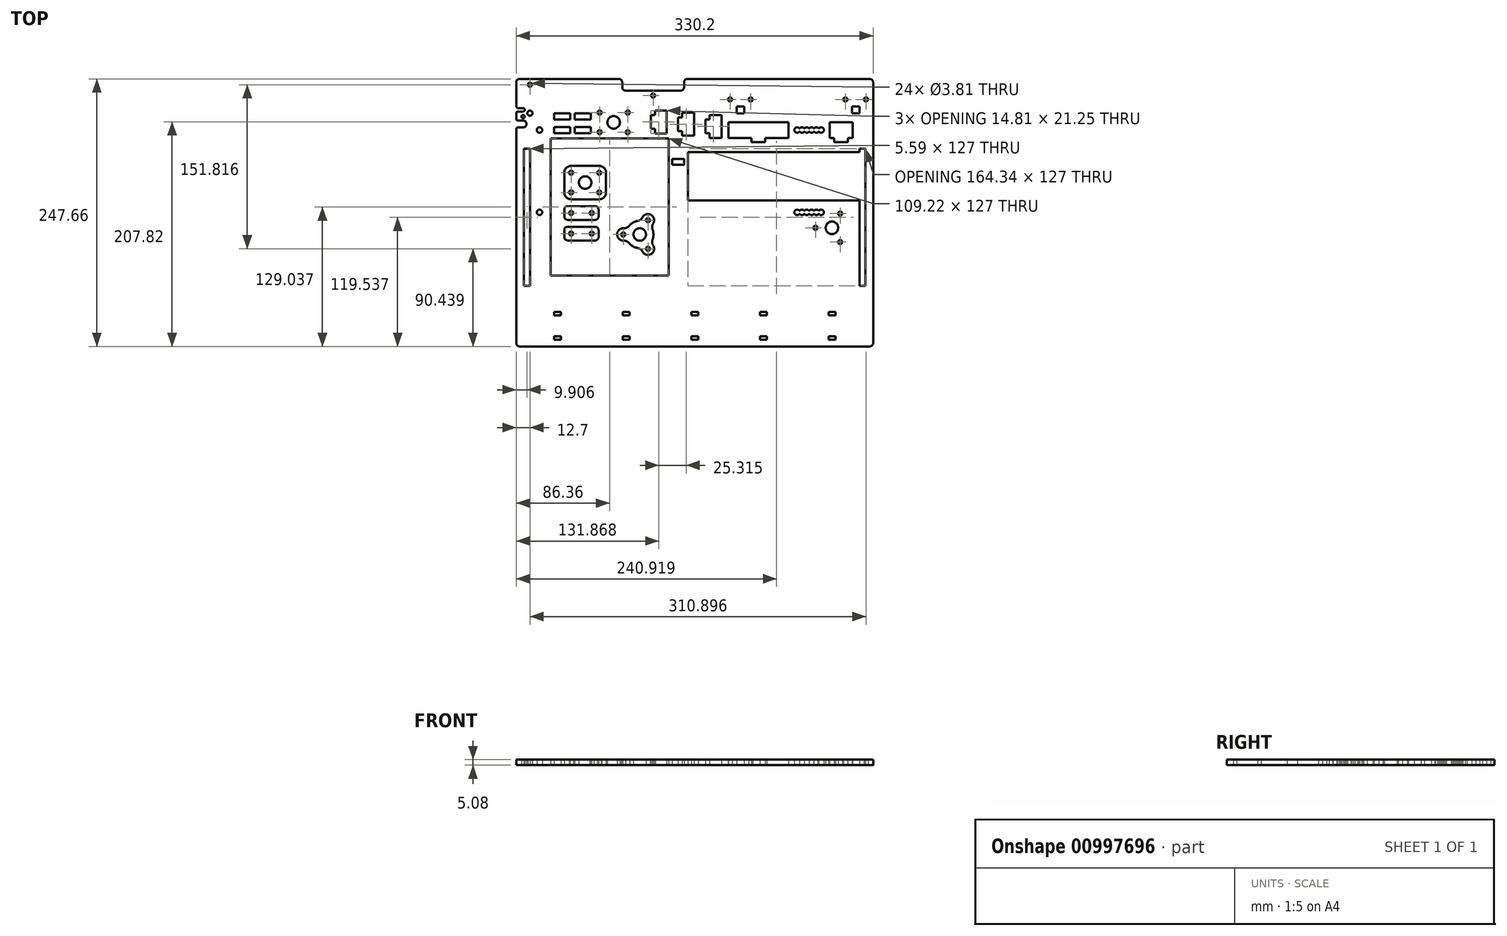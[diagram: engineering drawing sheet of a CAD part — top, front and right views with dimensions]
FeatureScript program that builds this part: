
annotation { "Feature Type Name" : "Feature", "Feature Type Description" : "" }
export const myFeature = defineFeature(function(context is Context, id is Id, definition is map)
    precondition{}
    {
        {
            var Q0;
            Q0=qCreatedBy(makeId("Top.planeOp"),FACE);
            var sketch = newSketch(context, id + "F0", { "sketchPlane" : qUnion([Q0])});
            skLineSegment(sketch, "E0.bottom", {"start": v(165.1, 111.12) * mm, "end": v(-165.1, 111.12) * mm, "construction": true});
            skLineSegment(sketch, "E0.top", {"start": v(161.93, -111.12) * mm, "end": v(-161.93, -111.12) * mm});
            skLineSegment(sketch, "E0.left", {"start": v(165.1, 111.13) * mm, "end": v(165.1, -107.95) * mm});
            skLineSegment(sketch, "E0.right", {"start": v(-165.1, 111.13) * mm, "end": v(-165.1, 111.12) * mm});
            skPoint(sketch, "E0.middle", {"position": v(0, 0) * mm});
            skLineSegment(sketch, "E1.bottom", {"start": v(86.87, 96.52) * mm, "end": v(31.15, 96.52) * mm});
            skLineSegment(sketch, "E1.top", {"start": v(86.87, 81.92) * mm, "end": v(65.36, 81.92) * mm});
            skLineSegment(sketch, "E1.left", {"start": v(86.87, 96.52) * mm, "end": v(86.87, 81.92) * mm});
            skLineSegment(sketch, "E1.right", {"start": v(31.15, 96.52) * mm, "end": v(31.15, 81.91) * mm});
            skPoint(sketch, "E1.middle", {"position": v(59.01, 89.22) * mm});
            skLineSegment(sketch, "E2.bottom", {"start": v(146.05, 96.52) * mm, "end": v(124.97, 96.52) * mm});
            skLineSegment(sketch, "E2.top", {"start": v(146.05, 81.92) * mm, "end": v(141.86, 81.92) * mm});
            skLineSegment(sketch, "E2.left", {"start": v(146.05, 96.52) * mm, "end": v(146.05, 81.91) * mm});
            skLineSegment(sketch, "E2.right", {"start": v(124.97, 96.52) * mm, "end": v(124.97, 81.91) * mm});
            skPoint(sketch, "E2.middle", {"position": v(135.5, 89.22) * mm});
            skPoint(sketch, "E2.middle.positionSnap0", {"position": v(86.87, 89.22) * mm});
            skPoint(sketch, "E2.centerSnap0", {"position": v(86.87, 89.22) * mm});
            skLineSegment(sketch, "E3", {"start": v(52.66, 81.91) * mm, "end": v(52.66, 78.1) * mm});
            skLineSegment(sketch, "E4", {"start": v(52.66, 78.1) * mm, "end": v(65.36, 78.1) * mm});
            skLineSegment(sketch, "E5", {"start": v(65.36, 78.1) * mm, "end": v(65.36, 81.91) * mm});
            skPoint(sketch, "E6", {"position": v(59.01, 78.1) * mm});
            skLineSegment(sketch, "E7", {"start": v(59.01, 96.52) * mm, "end": v(59.01, 78.1) * mm, "construction": true});
            skLineSegment(sketch, "E8", {"start": v(129.16, 81.91) * mm, "end": v(129.16, 78.1) * mm});
            skLineSegment(sketch, "E9", {"start": v(129.16, 78.1) * mm, "end": v(141.86, 78.1) * mm});
            skLineSegment(sketch, "E10", {"start": v(141.86, 78.1) * mm, "end": v(141.86, 81.91) * mm});
            skLineSegment(sketch, "E11", {"start": v(135.5, 78.1) * mm, "end": v(135.5, 96.52) * mm, "construction": true});
            skLineSegment(sketch, "E12.trimOffspring", {"start": v(52.66, 81.92) * mm, "end": v(31.15, 81.92) * mm});
            skLineSegment(sketch, "E13.trimOffspring", {"start": v(129.16, 81.92) * mm, "end": v(124.97, 81.92) * mm});
            skLineSegment(sketch, "E14", {"start": v(52.66, 81.92) * mm, "end": v(65.36, 81.92) * mm, "construction": true});
            skLineSegment(sketch, "E15", {"start": v(129.16, 81.92) * mm, "end": v(141.86, 81.92) * mm, "construction": true});
            skLineSegment(sketch, "E16.bottom", {"start": v(152.4, 68.7) * mm, "end": v(-6.35, 68.7) * mm});
            skLineSegment(sketch, "E16.top", {"start": v(152.4, 24.1) * mm, "end": v(-6.35, 24.1) * mm});
            skLineSegment(sketch, "E16.left", {"start": v(152.4, 68.7) * mm, "end": v(152.4, 24.1) * mm, "construction": true});
            skPoint(sketch, "E16.middle", {"position": v(73.02, 46.4) * mm});
            skLineSegment(sketch, "E17", {"start": v(-6.35, 68.7) * mm, "end": v(-6.35, 24.1) * mm});
            skArc(sketch, "E18", {"start": v(97.03, 90.45) * mm, "mid": v(92.27, 89.22) * mm, "end": v(97.03, 87.99) * mm});
            skArc(sketch, "E19.1.0.0", {"start": v(97.03, 87.99) * mm, "mid": v(99.25, 86.68) * mm, "end": v(101.47, 87.99) * mm});
            skArc(sketch, "E19.2.0.0", {"start": v(101.47, 87.99) * mm, "mid": v(103.7, 86.68) * mm, "end": v(105.92, 87.99) * mm});
            skArc(sketch, "E19.3.0.0", {"start": v(105.92, 87.99) * mm, "mid": v(108.14, 86.68) * mm, "end": v(110.36, 87.99) * mm});
            skArc(sketch, "E19.4.0.0", {"start": v(110.36, 87.99) * mm, "mid": v(112.59, 86.68) * mm, "end": v(114.8, 87.99) * mm});
            skArc(sketch, "E19.5.0.0", {"start": v(114.8, 87.99) * mm, "mid": v(119.57, 89.22) * mm, "end": v(114.8, 90.45) * mm});
            skLineSegment(sketch, "E19.direction1", {"start": v(94.8, 89.22) * mm, "end": v(99.25, 89.22) * mm, "construction": true});
            skLineSegment(sketch, "E20", {"start": v(94.8, 89.22) * mm, "end": v(117.03, 89.22) * mm, "construction": true});
            skArc(sketch, "E21.trimOffspring", {"start": v(101.47, 90.45) * mm, "mid": v(99.25, 91.76) * mm, "end": v(97.03, 90.45) * mm});
            skArc(sketch, "E22.trimOffspring", {"start": v(105.92, 90.45) * mm, "mid": v(103.7, 91.76) * mm, "end": v(101.47, 90.45) * mm});
            skArc(sketch, "E23.trimOffspring", {"start": v(110.36, 90.45) * mm, "mid": v(108.14, 91.76) * mm, "end": v(105.92, 90.45) * mm});
            skArc(sketch, "E24.trimOffspring", {"start": v(114.8, 90.45) * mm, "mid": v(112.59, 91.76) * mm, "end": v(110.36, 90.45) * mm});
            skPoint(sketch, "E25", {"position": v(105.92, 89.22) * mm});
            skArc(sketch, "E26.1.0.0", {"start": v(114.8, 14.25) * mm, "mid": v(112.59, 15.56) * mm, "end": v(110.36, 14.25) * mm});
            skArc(sketch, "E26.1.0.1", {"start": v(97.03, 14.25) * mm, "mid": v(92.27, 13.02) * mm, "end": v(97.03, 11.79) * mm});
            skLineSegment(sketch, "E26.1.0.2", {"start": v(94.8, 13.02) * mm, "end": v(117.03, 13.02) * mm, "construction": true});
            skArc(sketch, "E26.1.0.3", {"start": v(105.92, 14.25) * mm, "mid": v(103.7, 15.56) * mm, "end": v(101.47, 14.25) * mm});
            skArc(sketch, "E26.1.0.4", {"start": v(110.36, 11.79) * mm, "mid": v(112.59, 10.48) * mm, "end": v(114.8, 11.79) * mm});
            skArc(sketch, "E26.1.0.5", {"start": v(114.8, 11.79) * mm, "mid": v(119.57, 13.02) * mm, "end": v(114.8, 14.25) * mm});
            skArc(sketch, "E26.1.0.6", {"start": v(97.03, 11.79) * mm, "mid": v(99.25, 10.48) * mm, "end": v(101.47, 11.79) * mm});
            skPoint(sketch, "E26.1.0.7", {"position": v(105.92, 13.02) * mm});
            skArc(sketch, "E26.1.0.8", {"start": v(110.36, 14.25) * mm, "mid": v(108.14, 15.56) * mm, "end": v(105.92, 14.25) * mm});
            skLineSegment(sketch, "E26.1.0.9", {"start": v(94.8, 13.02) * mm, "end": v(99.25, 13.02) * mm, "construction": true});
            skArc(sketch, "E26.1.0.10", {"start": v(101.47, 11.79) * mm, "mid": v(103.7, 10.48) * mm, "end": v(105.92, 11.79) * mm});
            skArc(sketch, "E26.1.0.11", {"start": v(105.92, 11.79) * mm, "mid": v(108.14, 10.48) * mm, "end": v(110.36, 11.79) * mm});
            skArc(sketch, "E26.1.0.12", {"start": v(101.47, 14.25) * mm, "mid": v(99.25, 15.56) * mm, "end": v(97.03, 14.25) * mm});
            skLineSegment(sketch, "E26.direction1", {"start": v(94.8, 89.22) * mm, "end": v(94.8, 13.02) * mm, "construction": true});
            skLineSegment(sketch, "E27", {"start": v(94.8, 89.22) * mm, "end": v(86.87, 89.22) * mm, "construction": true});
            skLineSegment(sketch, "E28.bottom", {"start": v(-24.13, 81.4) * mm, "end": v(-133.35, 81.4) * mm});
            skLineSegment(sketch, "E28.top", {"start": v(-24.13, -45.6) * mm, "end": v(-133.35, -45.6) * mm});
            skLineSegment(sketch, "E28.left", {"start": v(-24.13, 81.4) * mm, "end": v(-24.13, -45.6) * mm});
            skLineSegment(sketch, "E28.right", {"start": v(-133.35, 81.4) * mm, "end": v(-133.35, -45.6) * mm});
            skLineSegment(sketch, "E29", {"start": v(-165.1, 111.12) * mm, "end": v(-165.1, 133.35) * mm});
            skLineSegment(sketch, "E30", {"start": v(-161.93, 136.53) * mm, "end": v(-70.15, 136.53) * mm});
            skLineSegment(sketch, "E31", {"start": v(165.1, 133.35) * mm, "end": v(165.1, 111.12) * mm});
            skCircle(sketch, "E32", {"center": v(-152.4, 131.12) * mm, "radius": 1.9 * mm});
            skCircle(sketch, "E33", {"center": v(-38.4, 121.12) * mm, "radius": 1.9 * mm});
            skLineSegment(sketch, "E34", {"start": v(152.4, 68.7) * mm, "end": v(152.4, 71.9) * mm});
            skLineSegment(sketch, "E35", {"start": v(152.4, 71.9) * mm, "end": v(157.99, 71.9) * mm});
            skLineSegment(sketch, "E36", {"start": v(157.99, 71.9) * mm, "end": v(157.99, -55.1) * mm});
            skLineSegment(sketch, "E37", {"start": v(157.99, -55.1) * mm, "end": v(152.4, -55.1) * mm});
            skLineSegment(sketch, "E38", {"start": v(152.4, -55.1) * mm, "end": v(152.4, 24.1) * mm});
            skLineSegment(sketch, "E39.bottom", {"start": v(-157.99, 71.9) * mm, "end": v(-152.4, 71.9) * mm});
            skLineSegment(sketch, "E39.top", {"start": v(-157.99, -55.1) * mm, "end": v(-152.4, -55.1) * mm});
            skLineSegment(sketch, "E39.left", {"start": v(-157.99, 71.9) * mm, "end": v(-157.99, -55.1) * mm});
            skLineSegment(sketch, "E39.right", {"start": v(-152.4, 71.9) * mm, "end": v(-152.4, -55.1) * mm});
            skLineSegment(sketch, "E40", {"start": v(-152.4, -55.1) * mm, "end": v(152.4, -55.1) * mm, "construction": true});
            skCircle(sketch, "E41", {"center": v(-143.51, 89.22) * mm, "radius": 2.54 * mm});
            skCircle(sketch, "E42.1.0.0", {"center": v(-143.51, 13.02) * mm, "radius": 2.54 * mm});
            skLineSegment(sketch, "E42.direction1", {"start": v(-143.51, 89.22) * mm, "end": v(-143.51, 13.02) * mm, "construction": true});
            skLineSegment(sketch, "E43", {"start": v(-66.98, 133.35) * mm, "end": v(-66.98, 128.74) * mm});
            skLineSegment(sketch, "E44", {"start": v(-63.8, 125.57) * mm, "end": v(-13, 125.57) * mm});
            skLineSegment(sketch, "E45", {"start": v(-9.83, 128.75) * mm, "end": v(-9.83, 133.35) * mm});
            skPoint(sketch, "E46", {"position": v(-38.4, 125.57) * mm});
            skLineSegment(sketch, "E47", {"start": v(-38.4, 125.57) * mm, "end": v(-38.4, 121.12) * mm, "construction": true});
            skLineSegment(sketch, "E48.trimOffspring", {"start": v(-6.65, 136.53) * mm, "end": v(161.92, 136.53) * mm});
            skLineSegment(sketch, "E49", {"start": v(-66.98, 136.53) * mm, "end": v(-9.83, 136.53) * mm, "construction": true});
            skPoint(sketch, "E50.visualSharp", {"position": v(-165.1, 136.53) * mm});
            skArc(sketch, "E50.filletArc", {"start": v(-161.93, 136.52) * mm, "mid": v(-164.17, 135.6) * mm, "end": v(-165.1, 133.35) * mm});
            skPoint(sketch, "E51.visualSharp", {"position": v(-66.98, 136.53) * mm});
            skArc(sketch, "E51.filletArc", {"start": v(-66.98, 133.35) * mm, "mid": v(-67.9, 135.6) * mm, "end": v(-70.15, 136.53) * mm});
            skPoint(sketch, "E52.visualSharp", {"position": v(-66.98, 125.57) * mm});
            skArc(sketch, "E52.filletArc", {"start": v(-66.98, 128.74) * mm, "mid": v(-66.05, 126.5) * mm, "end": v(-63.8, 125.57) * mm});
            skPoint(sketch, "E53.visualSharp", {"position": v(-9.83, 125.57) * mm});
            skArc(sketch, "E53.filletArc", {"start": v(-13, 125.57) * mm, "mid": v(-10.75, 126.5) * mm, "end": v(-9.83, 128.75) * mm});
            skPoint(sketch, "E54.visualSharp", {"position": v(-9.83, 136.52) * mm});
            skArc(sketch, "E54.filletArc", {"start": v(-6.65, 136.52) * mm, "mid": v(-8.9, 135.6) * mm, "end": v(-9.83, 133.35) * mm});
            skPoint(sketch, "E55.visualSharp", {"position": v(165.1, 136.53) * mm});
            skArc(sketch, "E55.filletArc", {"start": v(165.1, 133.35) * mm, "mid": v(164.17, 135.6) * mm, "end": v(161.92, 136.53) * mm});
            skPoint(sketch, "E56.visualSharp", {"position": v(165.1, -111.12) * mm});
            skArc(sketch, "E56.filletArc", {"start": v(161.93, -111.12) * mm, "mid": v(164.17, -110.2) * mm, "end": v(165.1, -107.95) * mm});
            skPoint(sketch, "E57.visualSharp", {"position": v(-165.1, -111.12) * mm});
            skArc(sketch, "E57.filletArc", {"start": v(-165.1, -107.95) * mm, "mid": v(-164.17, -110.2) * mm, "end": v(-161.93, -111.12) * mm});
            skCircle(sketch, "E58", {"center": v(127, -1.3) * mm, "radius": 5.8 * mm});
            skCircle(sketch, "E59", {"center": v(-74.93, 96.27) * mm, "radius": 5.8 * mm});
            skCircle(sketch, "E60", {"center": v(134.62, 11.9) * mm, "radius": 1.9 * mm});
            skCircle(sketch, "E61", {"center": v(111.76, -1.3) * mm, "radius": 1.9 * mm});
            skCircle(sketch, "E62", {"center": v(134.62, -14.5) * mm, "radius": 1.9 * mm});
            skLineSegment(sketch, "E63", {"start": v(111.76, -1.3) * mm, "end": v(127, -1.3) * mm, "construction": true});
            skLineSegment(sketch, "E64", {"start": v(127, -1.3) * mm, "end": v(134.62, 11.9) * mm, "construction": true});
            skLineSegment(sketch, "E65", {"start": v(127, -1.3) * mm, "end": v(134.62, -14.5) * mm, "construction": true});
            skCircle(sketch, "E66", {"center": v(-87.93, 105.37) * mm, "radius": 1.9 * mm});
            skCircle(sketch, "E67", {"center": v(-87.93, 87.16) * mm, "radius": 1.9 * mm});
            skCircle(sketch, "E68", {"center": v(-61.93, 87.16) * mm, "radius": 1.9 * mm});
            skCircle(sketch, "E69", {"center": v(-61.93, 105.37) * mm, "radius": 1.9 * mm});
            skLineSegment(sketch, "E70", {"start": v(-87.93, 105.37) * mm, "end": v(-61.93, 87.16) * mm, "construction": true});
            skLineSegment(sketch, "E71", {"start": v(-87.93, 87.16) * mm, "end": v(-61.93, 105.37) * mm, "construction": true});
            skLineSegment(sketch, "E72", {"start": v(-74.93, 96.27) * mm, "end": v(-74.93, 111.12) * mm, "construction": true});
            skLineSegment(sketch, "E73", {"start": v(-87.93, 87.16) * mm, "end": v(-61.93, 87.16) * mm, "construction": true});
            skLineSegment(sketch, "E74", {"start": v(-87.93, 105.37) * mm, "end": v(-87.93, 87.16) * mm, "construction": true});
            skLineSegment(sketch, "E75.bottom", {"start": v(-130.17, 92.07) * mm, "end": v(-115.17, 92.07) * mm});
            skLineSegment(sketch, "E75.top", {"start": v(-130.17, 86.32) * mm, "end": v(-115.17, 86.32) * mm});
            skLineSegment(sketch, "E75.left", {"start": v(-130.18, 92.07) * mm, "end": v(-130.18, 86.32) * mm});
            skLineSegment(sketch, "E75.right", {"start": v(-115.17, 92.07) * mm, "end": v(-115.17, 86.32) * mm});
            skLineSegment(sketch, "E76.1.0.0", {"start": v(-111.12, 92.07) * mm, "end": v(-96.12, 92.07) * mm});
            skLineSegment(sketch, "E76.1.0.1", {"start": v(-96.12, 92.07) * mm, "end": v(-96.12, 86.32) * mm});
            skLineSegment(sketch, "E76.1.0.2", {"start": v(-111.12, 92.07) * mm, "end": v(-111.12, 86.32) * mm});
            skLineSegment(sketch, "E76.1.0.3", {"start": v(-111.12, 86.32) * mm, "end": v(-96.12, 86.32) * mm});
            skLineSegment(sketch, "E76.direction1", {"start": v(-130.17, 86.32) * mm, "end": v(-111.12, 86.32) * mm, "construction": true});
            skLineSegment(sketch, "E77.1.0.0", {"start": v(-111.12, 104.77) * mm, "end": v(-96.12, 104.77) * mm});
            skLineSegment(sketch, "E77.1.0.1", {"start": v(-130.17, 104.78) * mm, "end": v(-115.17, 104.78) * mm});
            skLineSegment(sketch, "E77.1.0.2", {"start": v(-111.12, 99.02) * mm, "end": v(-96.12, 99.02) * mm});
            skLineSegment(sketch, "E77.1.0.3", {"start": v(-130.17, 99.02) * mm, "end": v(-111.12, 99.02) * mm, "construction": true});
            skLineSegment(sketch, "E77.1.0.6", {"start": v(-130.17, 99.02) * mm, "end": v(-115.17, 99.02) * mm});
            skLineSegment(sketch, "E77.1.0.7", {"start": v(-96.12, 104.77) * mm, "end": v(-96.12, 99.02) * mm});
            skLineSegment(sketch, "E77.1.0.8", {"start": v(-130.18, 104.77) * mm, "end": v(-130.18, 99.02) * mm});
            skLineSegment(sketch, "E77.1.0.11", {"start": v(-111.12, 104.77) * mm, "end": v(-111.12, 99.02) * mm});
            skLineSegment(sketch, "E77.1.0.12", {"start": v(-115.17, 104.77) * mm, "end": v(-115.17, 99.02) * mm});
            skLineSegment(sketch, "E77.direction1", {"start": v(-130.18, 86.32) * mm, "end": v(-130.18, 99.02) * mm, "construction": true});
            skLineSegment(sketch, "E78.bottom", {"start": v(13.8, 103.17) * mm, "end": v(24.8, 103.17) * mm});
            skLineSegment(sketch, "E78.top", {"start": v(13.8, 81.92) * mm, "end": v(24.8, 81.92) * mm});
            skLineSegment(sketch, "E78.left", {"start": v(13.8, 103.16) * mm, "end": v(13.8, 98.89) * mm});
            skLineSegment(sketch, "E78.right", {"start": v(24.8, 103.16) * mm, "end": v(24.8, 81.91) * mm});
            skLineSegment(sketch, "E79", {"start": v(13.8, 98.89) * mm, "end": v(10, 98.89) * mm});
            skLineSegment(sketch, "E80", {"start": v(10, 98.89) * mm, "end": v(10, 86.19) * mm});
            skLineSegment(sketch, "E81", {"start": v(10, 86.19) * mm, "end": v(13.8, 86.19) * mm});
            skPoint(sketch, "E82", {"position": v(10, 92.54) * mm});
            skLineSegment(sketch, "E83", {"start": v(10, 92.54) * mm, "end": v(24.8, 92.54) * mm, "construction": true});
            skLineSegment(sketch, "E84.trimOffspring", {"start": v(13.8, 86.19) * mm, "end": v(13.8, 81.91) * mm});
            skLineSegment(sketch, "E85", {"start": v(13.8, 98.89) * mm, "end": v(13.8, 86.19) * mm, "construction": true});
            skLineSegment(sketch, "E86", {"start": v(24.8, 81.92) * mm, "end": v(31.15, 81.92) * mm, "construction": true});
            skLineSegment(sketch, "E87.1.0.0", {"start": v(-15.32, 88.26) * mm, "end": v(-11.51, 88.26) * mm});
            skLineSegment(sketch, "E87.1.0.1", {"start": v(-0.51, 105.24) * mm, "end": v(-0.51, 83.99) * mm});
            skLineSegment(sketch, "E87.1.0.2", {"start": v(-11.51, 88.26) * mm, "end": v(-11.51, 84) * mm});
            skLineSegment(sketch, "E87.1.0.3", {"start": v(-11.51, 83.99) * mm, "end": v(-0.51, 83.99) * mm});
            skLineSegment(sketch, "E87.1.0.4", {"start": v(-11.51, 100.96) * mm, "end": v(-15.32, 100.96) * mm});
            skLineSegment(sketch, "E87.1.0.5", {"start": v(-11.51, 100.97) * mm, "end": v(-11.51, 88.26) * mm, "construction": true});
            skLineSegment(sketch, "E87.1.0.6", {"start": v(-11.51, 105.24) * mm, "end": v(-0.51, 105.24) * mm});
            skLineSegment(sketch, "E87.1.0.7", {"start": v(-15.32, 100.97) * mm, "end": v(-15.32, 88.26) * mm});
            skLineSegment(sketch, "E87.1.0.8", {"start": v(-11.51, 105.24) * mm, "end": v(-11.51, 100.97) * mm});
            skPoint(sketch, "E87.1.0.9", {"position": v(-15.32, 94.61) * mm});
            skLineSegment(sketch, "E87.1.0.10", {"start": v(-15.32, 94.61) * mm, "end": v(-0.51, 94.61) * mm, "construction": true});
            skLineSegment(sketch, "E87.2.0.0", {"start": v(-40.64, 90.34) * mm, "end": v(-36.83, 90.34) * mm});
            skLineSegment(sketch, "E87.2.0.1", {"start": v(-25.83, 107.32) * mm, "end": v(-25.83, 86.06) * mm});
            skLineSegment(sketch, "E87.2.0.2", {"start": v(-36.83, 90.34) * mm, "end": v(-36.83, 86.07) * mm});
            skLineSegment(sketch, "E87.2.0.3", {"start": v(-36.83, 86.06) * mm, "end": v(-25.83, 86.06) * mm});
            skLineSegment(sketch, "E87.2.0.4", {"start": v(-36.83, 103.04) * mm, "end": v(-40.64, 103.04) * mm});
            skLineSegment(sketch, "E87.2.0.5", {"start": v(-36.83, 103.04) * mm, "end": v(-36.83, 90.34) * mm, "construction": true});
            skLineSegment(sketch, "E87.2.0.6", {"start": v(-36.83, 107.32) * mm, "end": v(-25.83, 107.32) * mm});
            skLineSegment(sketch, "E87.2.0.7", {"start": v(-40.64, 103.04) * mm, "end": v(-40.64, 90.34) * mm});
            skLineSegment(sketch, "E87.2.0.8", {"start": v(-36.83, 107.31) * mm, "end": v(-36.83, 103.04) * mm});
            skPoint(sketch, "E87.2.0.9", {"position": v(-40.64, 96.69) * mm});
            skLineSegment(sketch, "E87.2.0.10", {"start": v(-40.64, 96.69) * mm, "end": v(-25.83, 96.69) * mm, "construction": true});
            skLineSegment(sketch, "E87.direction1", {"start": v(13.8, 81.91) * mm, "end": v(-11.51, 83.99) * mm, "construction": true});
            skCircle(sketch, "E88", {"center": v(-101.3, 40.55) * mm, "radius": 5.8 * mm});
            skCircle(sketch, "E89", {"center": v(-114.3, 49.66) * mm, "radius": 1.9 * mm});
            skCircle(sketch, "E90", {"center": v(-114.3, 31.45) * mm, "radius": 1.9 * mm});
            skCircle(sketch, "E91", {"center": v(-88.3, 31.45) * mm, "radius": 1.9 * mm});
            skCircle(sketch, "E92", {"center": v(-88.3, 49.66) * mm, "radius": 1.9 * mm});
            skLineSegment(sketch, "E93", {"start": v(-114.3, 49.66) * mm, "end": v(-88.3, 31.45) * mm, "construction": true});
            skLineSegment(sketch, "E94", {"start": v(-114.3, 31.45) * mm, "end": v(-88.3, 49.66) * mm, "construction": true});
            skLineSegment(sketch, "E95", {"start": v(-114.3, 31.45) * mm, "end": v(-88.3, 31.45) * mm, "construction": true});
            skLineSegment(sketch, "E96", {"start": v(-114.3, 49.66) * mm, "end": v(-114.3, 31.45) * mm, "construction": true});
            skCircle(sketch, "E97", {"center": v(-50.8, -7.5) * mm, "radius": 5.8 * mm});
            skCircle(sketch, "E98", {"center": v(-43.18, 5.7) * mm, "radius": 1.9 * mm});
            skCircle(sketch, "E99", {"center": v(-66.04, -7.5) * mm, "radius": 1.9 * mm});
            skCircle(sketch, "E100", {"center": v(-43.18, -20.7) * mm, "radius": 1.9 * mm});
            skLineSegment(sketch, "E101", {"start": v(-66.04, -7.5) * mm, "end": v(-50.8, -7.5) * mm, "construction": true});
            skLineSegment(sketch, "E102", {"start": v(-50.8, -7.5) * mm, "end": v(-43.18, 5.7) * mm, "construction": true});
            skLineSegment(sketch, "E103", {"start": v(-50.8, -7.5) * mm, "end": v(-43.18, -20.7) * mm, "construction": true});
            skArc(sketch, "E104", {"start": v(-65.8, -1.78) * mm, "mid": v(-71.76, -7.5) * mm, "end": v(-65.8, -13.2) * mm});
            skArc(sketch, "E105", {"start": v(-38.35, 2.65) * mm, "mid": v(-40.32, 10.65) * mm, "end": v(-48.24, 8.36) * mm});
            skArc(sketch, "E106", {"start": v(-60.63, -15.53) * mm, "mid": v(-57.15, -18.5) * mm, "end": v(-52.84, -20.03) * mm});
            skArc(sketch, "E107", {"start": v(-48.24, -23.35) * mm, "mid": v(-40.32, -25.64) * mm, "end": v(-38.35, -17.64) * mm});
            skLineSegment(sketch, "E108.bottom", {"start": v(-88.3, 56) * mm, "end": v(-114.3, 56) * mm});
            skLineSegment(sketch, "E108.top", {"start": v(-88.3, 25.1) * mm, "end": v(-114.3, 25.1) * mm});
            skLineSegment(sketch, "E108.left", {"start": v(-81.94, 49.66) * mm, "end": v(-81.94, 31.45) * mm});
            skLineSegment(sketch, "E108.right", {"start": v(-120.65, 49.66) * mm, "end": v(-120.65, 31.45) * mm});
            skArc(sketch, "E109.trimOffspring", {"start": v(-38.92, -12) * mm, "mid": v(-38.1, -7.5) * mm, "end": v(-38.92, -3) * mm});
            skArc(sketch, "E110.trimOffspring", {"start": v(-52.84, 5.04) * mm, "mid": v(-57.15, 3.5) * mm, "end": v(-60.63, 0.54) * mm});
            skPoint(sketch, "E111.visualSharp", {"position": v(-62.64, -2.9) * mm});
            skArc(sketch, "E111.filletArc", {"start": v(-65.8, -1.78) * mm, "mid": v(-62.95, -1.23) * mm, "end": v(-60.63, 0.54) * mm});
            skPoint(sketch, "E112.visualSharp", {"position": v(-62.64, -12.09) * mm});
            skArc(sketch, "E112.filletArc", {"start": v(-60.63, -15.53) * mm, "mid": v(-62.95, -13.76) * mm, "end": v(-65.8, -13.2) * mm});
            skPoint(sketch, "E113.visualSharp", {"position": v(-48.86, -20.04) * mm});
            skArc(sketch, "E113.filletArc", {"start": v(-48.24, -23.35) * mm, "mid": v(-50.15, -21.14) * mm, "end": v(-52.84, -20.03) * mm});
            skPoint(sketch, "E114.visualSharp", {"position": v(-40.9, -15.45) * mm});
            skArc(sketch, "E114.filletArc", {"start": v(-38.92, -12) * mm, "mid": v(-39.3, -14.88) * mm, "end": v(-38.35, -17.64) * mm});
            skPoint(sketch, "E115.visualSharp", {"position": v(-40.9, 0.46) * mm});
            skArc(sketch, "E115.filletArc", {"start": v(-38.35, 2.65) * mm, "mid": v(-39.3, -0.1) * mm, "end": v(-38.92, -3) * mm});
            skPoint(sketch, "E116.visualSharp", {"position": v(-48.86, 5.06) * mm});
            skArc(sketch, "E116.filletArc", {"start": v(-52.84, 5.04) * mm, "mid": v(-50.15, 6.16) * mm, "end": v(-48.24, 8.36) * mm});
            skArc(sketch, "E117.filletArc", {"start": v(-81.94, 49.66) * mm, "mid": v(-83.8, 54.15) * mm, "end": v(-88.3, 56) * mm});
            skArc(sketch, "E118.filletArc", {"start": v(-88.3, 25.1) * mm, "mid": v(-83.8, 26.96) * mm, "end": v(-81.94, 31.45) * mm});
            skPoint(sketch, "E119.visualSharp", {"position": v(-120.65, 25.1) * mm});
            skArc(sketch, "E119.filletArc", {"start": v(-120.65, 31.45) * mm, "mid": v(-118.8, 26.96) * mm, "end": v(-114.3, 25.1) * mm});
            skPoint(sketch, "E120.visualSharp", {"position": v(-120.65, 56) * mm});
            skArc(sketch, "E120.filletArc", {"start": v(-114.3, 56) * mm, "mid": v(-118.8, 54.15) * mm, "end": v(-120.65, 49.66) * mm});
            skLineSegment(sketch, "E121", {"start": v(-101.3, 56) * mm, "end": v(-101.3, 40.55) * mm, "construction": true});
            skLineSegment(sketch, "E122.bottom", {"start": v(152.4, 111.12) * mm, "end": v(145.54, 111.12) * mm});
            skLineSegment(sketch, "E122.top", {"start": v(152.4, 104.78) * mm, "end": v(145.54, 104.78) * mm});
            skLineSegment(sketch, "E122.left", {"start": v(152.4, 111.13) * mm, "end": v(152.4, 104.78) * mm});
            skLineSegment(sketch, "E122.right", {"start": v(145.54, 111.13) * mm, "end": v(145.54, 104.78) * mm});
            skLineSegment(sketch, "E123.1.0.0", {"start": v(45.72, 104.78) * mm, "end": v(38.86, 104.78) * mm});
            skLineSegment(sketch, "E123.1.0.1", {"start": v(45.72, 111.13) * mm, "end": v(45.72, 104.78) * mm});
            skLineSegment(sketch, "E123.1.0.2", {"start": v(38.86, 111.13) * mm, "end": v(38.86, 104.78) * mm});
            skLineSegment(sketch, "E123.1.0.3", {"start": v(45.72, 111.12) * mm, "end": v(38.86, 111.12) * mm});
            skLineSegment(sketch, "E123.direction1", {"start": v(145.54, 104.78) * mm, "end": v(38.86, 104.78) * mm, "construction": true});
            skCircle(sketch, "E124", {"center": v(32.77, 117.48) * mm, "radius": 1.9 * mm});
            skCircle(sketch, "E125", {"center": v(51.82, 117.48) * mm, "radius": 1.9 * mm});
            skLineSegment(sketch, "E126", {"start": v(32.77, 117.48) * mm, "end": v(51.82, 117.48) * mm, "construction": true});
            skLineSegment(sketch, "E127", {"start": v(42.3, 117.48) * mm, "end": v(42.3, 104.78) * mm, "construction": true});
            skCircle(sketch, "E128", {"center": v(139.45, 117.48) * mm, "radius": 1.9 * mm});
            skCircle(sketch, "E129", {"center": v(158.5, 117.48) * mm, "radius": 1.9 * mm});
            skLineSegment(sketch, "E130", {"start": v(139.45, 117.48) * mm, "end": v(158.5, 117.48) * mm, "construction": true});
            skLineSegment(sketch, "E131", {"start": v(148.97, 117.48) * mm, "end": v(148.97, 104.78) * mm, "construction": true});
            skLineSegment(sketch, "E132.bottom", {"start": v(-117.47, 18.75) * mm, "end": v(-92.07, 18.75) * mm});
            skLineSegment(sketch, "E132.left", {"start": v(-120.65, 15.57) * mm, "end": v(-120.65, 9.22) * mm});
            skLineSegment(sketch, "E132.right", {"start": v(-88.9, 15.57) * mm, "end": v(-88.9, 9.22) * mm});
            skCircle(sketch, "E133", {"center": v(-114.3, 12.4) * mm, "radius": 1.9 * mm});
            skCircle(sketch, "E134", {"center": v(-95.25, 12.4) * mm, "radius": 1.9 * mm});
            skLineSegment(sketch, "E135", {"start": v(-114.3, 12.4) * mm, "end": v(-95.25, 12.4) * mm, "construction": true});
            skLineSegment(sketch, "E136", {"start": v(-95.25, 6.05) * mm, "end": v(-95.25, 12.4) * mm, "construction": true});
            skPoint(sketch, "E137.visualSharp", {"position": v(-120.65, 18.75) * mm});
            skArc(sketch, "E137.filletArc", {"start": v(-117.47, 18.75) * mm, "mid": v(-119.72, 17.82) * mm, "end": v(-120.65, 15.57) * mm});
            skPoint(sketch, "E138.visualSharp", {"position": v(-88.9, 18.75) * mm});
            skArc(sketch, "E138.filletArc", {"start": v(-88.9, 15.57) * mm, "mid": v(-89.83, 17.82) * mm, "end": v(-92.07, 18.75) * mm});
            skArc(sketch, "E139.filletArc", {"start": v(-120.65, 9.22) * mm, "mid": v(-119.72, 6.98) * mm, "end": v(-117.47, 6.05) * mm});
            skArc(sketch, "E140.filletArc", {"start": v(-92.07, 6.05) * mm, "mid": v(-89.83, 6.98) * mm, "end": v(-88.9, 9.22) * mm});
            skLineSegment(sketch, "E141", {"start": v(-88.9, 6.05) * mm, "end": v(-88.9, 18.75) * mm, "construction": true});
            skLineSegment(sketch, "E142", {"start": v(-120.65, 18.75) * mm, "end": v(-88.9, 18.75) * mm, "construction": true});
            skLineSegment(sketch, "E143", {"start": v(-117.47, 6.05) * mm, "end": v(-92.07, 6.05) * mm});
            skLineSegment(sketch, "E144", {"start": v(-92.07, 6.05) * mm, "end": v(-88.9, 6.05) * mm, "construction": true});
            skLineSegment(sketch, "E145", {"start": v(-117.47, 6.05) * mm, "end": v(-120.65, 6.05) * mm, "construction": true});
            skLineSegment(sketch, "E146", {"start": v(-120.65, 6.05) * mm, "end": v(-120.65, 9.22) * mm, "construction": true});
            skArc(sketch, "E147.1.0.0", {"start": v(-120.65, -9.83) * mm, "mid": v(-119.72, -12.07) * mm, "end": v(-117.47, -13) * mm});
            skArc(sketch, "E147.1.0.1", {"start": v(-92.07, -13) * mm, "mid": v(-89.83, -12.07) * mm, "end": v(-88.9, -9.83) * mm});
            skLineSegment(sketch, "E147.1.0.2", {"start": v(-117.47, -13) * mm, "end": v(-92.07, -13) * mm});
            skLineSegment(sketch, "E147.1.0.3", {"start": v(-120.65, -3.48) * mm, "end": v(-120.65, -9.83) * mm});
            skArc(sketch, "E147.1.0.4", {"start": v(-117.47, -0.3) * mm, "mid": v(-119.72, -1.23) * mm, "end": v(-120.65, -3.48) * mm});
            skPoint(sketch, "E147.1.0.5", {"position": v(-120.65, -0.3) * mm});
            skCircle(sketch, "E147.1.0.6", {"center": v(-95.25, -6.65) * mm, "radius": 1.9 * mm});
            skArc(sketch, "E147.1.0.7", {"start": v(-88.9, -3.48) * mm, "mid": v(-89.83, -1.23) * mm, "end": v(-92.07, -0.3) * mm});
            skCircle(sketch, "E147.1.0.8", {"center": v(-114.3, -6.65) * mm, "radius": 1.9 * mm});
            skPoint(sketch, "E147.1.0.9", {"position": v(-88.9, -0.3) * mm});
            skLineSegment(sketch, "E147.1.0.10", {"start": v(-88.9, -3.48) * mm, "end": v(-88.9, -9.83) * mm});
            skLineSegment(sketch, "E147.1.0.11", {"start": v(-117.47, -0.3) * mm, "end": v(-92.07, -0.3) * mm});
            skLineSegment(sketch, "E147.direction1", {"start": v(-117.47, 6.05) * mm, "end": v(-117.47, -13) * mm, "construction": true});
            skLineSegment(sketch, "E148.bottom", {"start": v(-20.7, 62.36) * mm, "end": v(-9.78, 62.36) * mm});
            skLineSegment(sketch, "E148.top", {"start": v(-20.7, 57.02) * mm, "end": v(-9.78, 57.02) * mm});
            skLineSegment(sketch, "E148.left", {"start": v(-20.7, 62.36) * mm, "end": v(-20.7, 57.02) * mm});
            skLineSegment(sketch, "E148.right", {"start": v(-9.78, 62.36) * mm, "end": v(-9.78, 57.02) * mm});
            skPoint(sketch, "E149", {"position": v(-15.24, 62.36) * mm});
            skCircle(sketch, "E150", {"center": v(-158.75, 101.6) * mm, "radius": 1.5 * mm});
            skLineSegment(sketch, "E151", {"start": v(-163.51, 109.54) * mm, "end": v(-158.75, 109.54) * mm});
            skLineSegment(sketch, "E152", {"start": v(-158.75, 106.36) * mm, "end": v(-163.51, 106.36) * mm});
            skLineSegment(sketch, "E153", {"start": v(-158.75, 101.6) * mm, "end": v(-158.75, 107.95) * mm, "construction": true});
            skArc(sketch, "E154", {"start": v(-158.75, 106.36) * mm, "mid": v(-157.16, 107.95) * mm, "end": v(-158.75, 109.54) * mm});
            skLineSegment(sketch, "E155.trimOffspring", {"start": v(-165.1, 104.78) * mm, "end": v(-165.1, 99.5) * mm});
            skPoint(sketch, "E156.visualSharp", {"position": v(-165.1, 109.54) * mm});
            skArc(sketch, "E156.filletArc", {"start": v(-165.1, 111.12) * mm, "mid": v(-164.64, 110) * mm, "end": v(-163.51, 109.54) * mm});
            skPoint(sketch, "E157.visualSharp", {"position": v(-165.1, 106.36) * mm});
            skLineSegment(sketch, "E158", {"start": v(-157.99, 71.9) * mm, "end": v(-157.99, 89.69) * mm, "construction": true});
            skCircle(sketch, "E159", {"center": v(-152.4, 104.78) * mm, "radius": 2.38 * mm});
            skLineSegment(sketch, "E160", {"start": v(-158.75, 104.78) * mm, "end": v(-152.4, 104.78) * mm, "construction": true});
            skLineSegment(sketch, "E161", {"start": v(-163.51, 97.92) * mm, "end": v(-158.75, 97.92) * mm});
            skLineSegment(sketch, "E162", {"start": v(-163.51, 91.57) * mm, "end": v(-158.75, 91.57) * mm});
            skLineSegment(sketch, "E163.trimOffspring", {"start": v(-165.1, 89.98) * mm, "end": v(-165.1, -107.95) * mm});
            skArc(sketch, "E164", {"start": v(-158.75, 91.57) * mm, "mid": v(-155.58, 94.74) * mm, "end": v(-158.75, 97.92) * mm});
            skPoint(sketch, "E165.visualSharp", {"position": v(-165.1, 91.57) * mm});
            skArc(sketch, "E165.filletArc", {"start": v(-163.51, 91.57) * mm, "mid": v(-164.64, 91.1) * mm, "end": v(-165.1, 89.98) * mm});
            skLineSegment(sketch, "E166", {"start": v(-158.75, 94.74) * mm, "end": v(-158.75, 101.6) * mm, "construction": true});
            skArc(sketch, "E167.filletArc", {"start": v(-163.51, 106.36) * mm, "mid": v(-164.64, 105.9) * mm, "end": v(-165.1, 104.78) * mm});
            skPoint(sketch, "E168.visualSharp", {"position": v(-165.1, 97.92) * mm});
            skArc(sketch, "E168.filletArc", {"start": v(-165.1, 99.5) * mm, "mid": v(-164.64, 98.38) * mm, "end": v(-163.51, 97.92) * mm});
            skLineSegment(sketch, "E169.bottom", {"start": v(3.17, -79.24) * mm, "end": v(-3.18, -79.24) * mm});
            skLineSegment(sketch, "E169.top", {"start": v(3.17, -82.41) * mm, "end": v(-3.17, -82.41) * mm});
            skLineSegment(sketch, "E169.left", {"start": v(3.17, -79.24) * mm, "end": v(3.17, -82.41) * mm});
            skLineSegment(sketch, "E169.right", {"start": v(-3.18, -79.24) * mm, "end": v(-3.18, -82.41) * mm});
            skPoint(sketch, "E169.middle", {"position": v(0, -80.83) * mm});
            skLineSegment(sketch, "E170.0.1.0", {"start": v(3.17, -101.74) * mm, "end": v(-3.17, -101.74) * mm});
            skLineSegment(sketch, "E170.0.1.1", {"start": v(3.18, -101.74) * mm, "end": v(3.18, -104.91) * mm});
            skLineSegment(sketch, "E170.0.1.2", {"start": v(3.17, -104.91) * mm, "end": v(-3.17, -104.91) * mm});
            skLineSegment(sketch, "E170.0.1.3", {"start": v(-3.17, -101.74) * mm, "end": v(-3.17, -104.91) * mm});
            skLineSegment(sketch, "E170.1.0.0", {"start": v(66.67, -79.24) * mm, "end": v(60.32, -79.24) * mm});
            skLineSegment(sketch, "E170.1.0.1", {"start": v(66.67, -79.24) * mm, "end": v(66.67, -82.41) * mm});
            skLineSegment(sketch, "E170.1.0.2", {"start": v(66.67, -82.41) * mm, "end": v(60.33, -82.41) * mm});
            skLineSegment(sketch, "E170.1.0.3", {"start": v(60.33, -79.24) * mm, "end": v(60.33, -82.41) * mm});
            skLineSegment(sketch, "E170.1.1.0", {"start": v(66.67, -101.74) * mm, "end": v(60.32, -101.74) * mm});
            skLineSegment(sketch, "E170.1.1.1", {"start": v(66.68, -101.74) * mm, "end": v(66.68, -104.91) * mm});
            skLineSegment(sketch, "E170.1.1.2", {"start": v(66.67, -104.91) * mm, "end": v(60.33, -104.91) * mm});
            skLineSegment(sketch, "E170.1.1.3", {"start": v(60.33, -101.74) * mm, "end": v(60.33, -104.91) * mm});
            skLineSegment(sketch, "E170.2.0.0", {"start": v(130.17, -79.24) * mm, "end": v(123.82, -79.24) * mm});
            skLineSegment(sketch, "E170.2.0.1", {"start": v(130.18, -79.24) * mm, "end": v(130.18, -82.41) * mm});
            skLineSegment(sketch, "E170.2.0.2", {"start": v(130.17, -82.41) * mm, "end": v(123.83, -82.41) * mm});
            skLineSegment(sketch, "E170.2.0.3", {"start": v(123.83, -79.24) * mm, "end": v(123.83, -82.41) * mm});
            skLineSegment(sketch, "E170.2.1.0", {"start": v(130.17, -101.74) * mm, "end": v(123.82, -101.74) * mm});
            skLineSegment(sketch, "E170.2.1.1", {"start": v(130.18, -101.74) * mm, "end": v(130.18, -104.91) * mm});
            skLineSegment(sketch, "E170.2.1.2", {"start": v(130.17, -104.91) * mm, "end": v(123.83, -104.91) * mm});
            skLineSegment(sketch, "E170.2.1.3", {"start": v(123.83, -101.74) * mm, "end": v(123.83, -104.91) * mm});
            skLineSegment(sketch, "E170.direction1", {"start": v(3.17, -79.24) * mm, "end": v(66.67, -79.24) * mm, "construction": true});
            skLineSegment(sketch, "E170.direction2", {"start": v(3.18, -79.24) * mm, "end": v(3.18, -101.74) * mm, "construction": true});
            skLineSegment(sketch, "E171", {"start": v(0, -82.41) * mm, "end": v(0, -101.74) * mm, "construction": true});
            skPoint(sketch, "E172", {"position": v(0, -92.08) * mm});
            skLineSegment(sketch, "E173.1.0.0", {"start": v(-66.67, -101.74) * mm, "end": v(-66.67, -104.91) * mm});
            skLineSegment(sketch, "E173.1.0.1", {"start": v(-60.33, -79.24) * mm, "end": v(-66.67, -79.24) * mm});
            skLineSegment(sketch, "E173.1.0.2", {"start": v(-60.33, -82.41) * mm, "end": v(-66.67, -82.41) * mm});
            skLineSegment(sketch, "E173.1.0.3", {"start": v(-66.67, -79.24) * mm, "end": v(-66.67, -82.41) * mm});
            skLineSegment(sketch, "E173.1.0.4", {"start": v(-60.32, -101.74) * mm, "end": v(-60.32, -104.91) * mm});
            skLineSegment(sketch, "E173.1.0.5", {"start": v(-60.33, -104.91) * mm, "end": v(-66.67, -104.91) * mm});
            skLineSegment(sketch, "E173.1.0.6", {"start": v(-60.33, -101.74) * mm, "end": v(-66.67, -101.74) * mm});
            skLineSegment(sketch, "E173.1.0.7", {"start": v(-60.32, -79.24) * mm, "end": v(-60.32, -82.41) * mm});
            skLineSegment(sketch, "E173.2.0.0", {"start": v(-130.17, -101.74) * mm, "end": v(-130.17, -104.91) * mm});
            skLineSegment(sketch, "E173.2.0.1", {"start": v(-123.83, -79.24) * mm, "end": v(-130.18, -79.24) * mm});
            skLineSegment(sketch, "E173.2.0.2", {"start": v(-123.83, -82.41) * mm, "end": v(-130.17, -82.41) * mm});
            skLineSegment(sketch, "E173.2.0.3", {"start": v(-130.18, -79.24) * mm, "end": v(-130.18, -82.41) * mm});
            skLineSegment(sketch, "E173.2.0.4", {"start": v(-123.82, -101.74) * mm, "end": v(-123.82, -104.91) * mm});
            skLineSegment(sketch, "E173.2.0.5", {"start": v(-123.83, -104.91) * mm, "end": v(-130.17, -104.91) * mm});
            skLineSegment(sketch, "E173.2.0.6", {"start": v(-123.83, -101.74) * mm, "end": v(-130.17, -101.74) * mm});
            skLineSegment(sketch, "E173.2.0.7", {"start": v(-123.82, -79.24) * mm, "end": v(-123.82, -82.41) * mm});
            skLineSegment(sketch, "E173.direction1", {"start": v(-3.17, -79.24) * mm, "end": v(-66.67, -79.24) * mm, "construction": true});
            skSolve(sketch);
        }
        {
            var Q0;
            Q0=makeQuery(id+"F0.imprint","IMPRINT",FACE,{"disambiguationData":[TD([[makeQuery(id+"F0.imprint","IMPRINT",EDGE,{"derivedFrom":sQuery(id+"F0.wireOp",EDGE,"E0.top")}),-1.0]])]});
            var Q1;
            Q1=makeQuery(id+"F0.imprint","IMPRINT",FACE,{"disambiguationData":[TD([[makeQuery(id+"F0.imprint","IMPRINT",EDGE,{"derivedFrom":sQuery(id+"F0.wireOp",EDGE,"E88")}),-1.0]])]});
            var Q2;
            Q2=makeQuery(id+"F0.imprint","IMPRINT",FACE,{"disambiguationData":[TD([[makeQuery(id+"F0.imprint","IMPRINT",EDGE,{"derivedFrom":sQuery(id+"F0.wireOp",EDGE,"E132.bottom")}),-1.0]])]});
            var Q3;
            Q3=makeQuery(id+"F0.imprint","IMPRINT",FACE,{"disambiguationData":[TD([[makeQuery(id+"F0.imprint","IMPRINT",EDGE,{"derivedFrom":sQuery(id+"F0.wireOp",EDGE,"E147.1.0.0")}),1.0]])]});
            var Q4;
            Q4=makeQuery(id+"F0.imprint","IMPRINT",FACE,{"disambiguationData":[TD([[makeQuery(id+"F0.imprint","IMPRINT",EDGE,{"derivedFrom":sQuery(id+"F0.wireOp",EDGE,"E97")}),-1.0]])]});
            var Q5;
            Q5=makeQuery(id+"F0.imprint","IMPRINT",FACE,{"disambiguationData":[TD([[makeQuery(id+"F0.imprint","IMPRINT",EDGE,{"derivedFrom":sQuery(id+"F0.wireOp",EDGE,"ExwOmx0V-QpKa-uj60-LMiD-LbWv7r9h28dm.bottom")}),-1.0]])]});
            var Q6;
            Q6=makeQuery(id+"F0.imprint","IMPRINT",FACE,{"disambiguationData":[TD([[makeQuery(id+"F0.imprint","IMPRINT",EDGE,{"derivedFrom":sQuery(id+"F0.wireOp",EDGE,"d1386968-dacd-495b-a7e0-b55d14b1c3aa.1.0.0")}),1.0]])]});
            var Q7;
            Q7=makeQuery(id+"F0.imprint","IMPRINT",FACE,{"disambiguationData":[TD([[makeQuery(id+"F0.imprint","IMPRINT",EDGE,{"derivedFrom":sQuery(id+"F0.wireOp",EDGE,"d1386968-dacd-495b-a7e0-b55d14b1c3aa.2.0.0")}),1.0]])]});
            var Q8;
            Q8=makeQuery(id+"F0.imprint","IMPRINT",FACE,{"disambiguationData":[TD([[makeQuery(id+"F0.imprint","IMPRINT",EDGE,{"derivedFrom":sQuery(id+"F0.wireOp",EDGE,"9cb2db9c-734c-4b5a-86ab-4ed233e76aa2.0.1.0")}),1.0]])]});
            var Q9;
            Q9=makeQuery(id+"F0.imprint","IMPRINT",FACE,{"disambiguationData":[TD([[makeQuery(id+"F0.imprint","IMPRINT",EDGE,{"derivedFrom":sQuery(id+"F0.wireOp",EDGE,"9cb2db9c-734c-4b5a-86ab-4ed233e76aa2.1.1.0")}),1.0]])]});
            var Q10;
            Q10=makeQuery(id+"F0.imprint","IMPRINT",FACE,{"disambiguationData":[TD([[makeQuery(id+"F0.imprint","IMPRINT",EDGE,{"derivedFrom":sQuery(id+"F0.wireOp",EDGE,"CqBNxeBT-CJMC-ExP6-8SwA-7D1fpahWLce3")}),1.0]])]});
            var Q11;
            Q11=makeQuery(id+"F0.imprint","IMPRINT",FACE,{"disambiguationData":[TD([[makeQuery(id+"F0.imprint","IMPRINT",EDGE,{"derivedFrom":sQuery(id+"F0.wireOp",EDGE,"9cb2db9c-734c-4b5a-86ab-4ed233e76aa2.1.0.0")}),1.0]])]});
            var Q12;
            Q12=makeQuery(id+"F0.imprint","IMPRINT",FACE,{"disambiguationData":[TD([[makeQuery(id+"F0.imprint","IMPRINT",EDGE,{"derivedFrom":sQuery(id+"F0.wireOp",EDGE,"D8P29blQ-q5rL-KMrv-Kh3W-neXXSiCKrR4P")}),1.0]])]});
            extrude(context, id + "F1", {"entities" : qUnion([Q0, Q1, Q2, Q3, Q4, Q5, Q6, Q7, Q8, Q9, Q10, Q11, Q12]), "depth" : 5.08 * mm, "offsetDistance" : 25.4 * mm});
        }
    });
